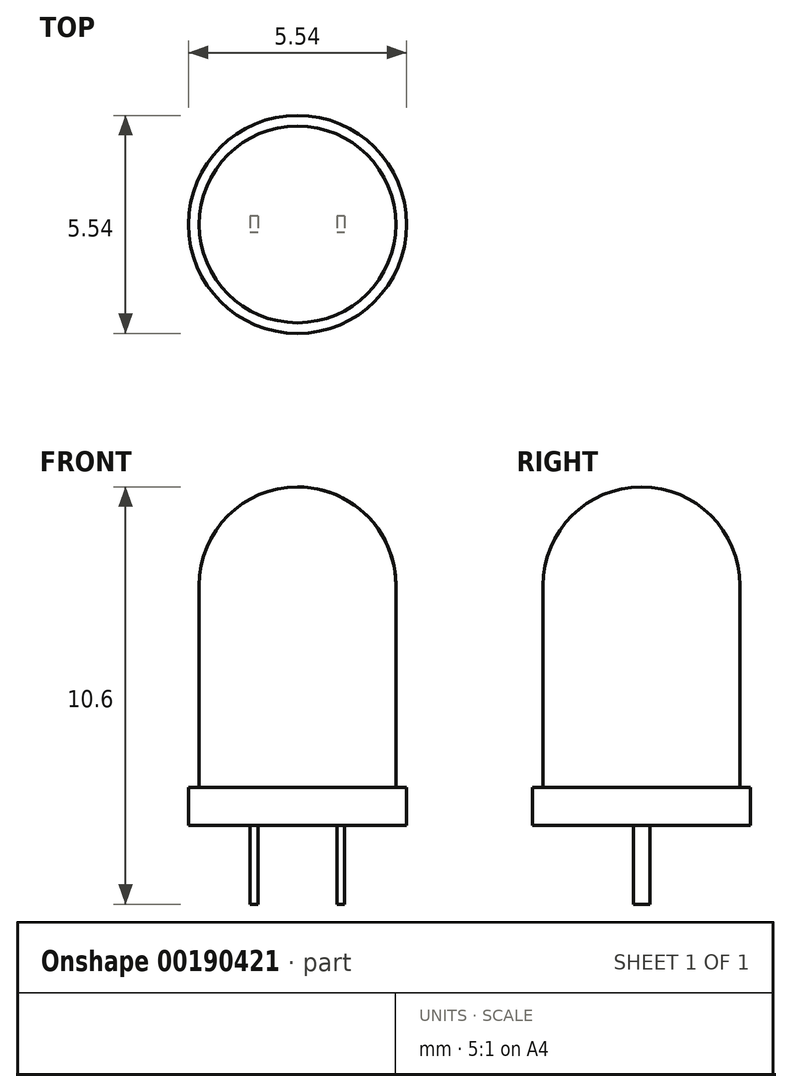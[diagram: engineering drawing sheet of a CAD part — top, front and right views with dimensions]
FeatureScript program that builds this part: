
annotation { "Feature Type Name" : "Feature", "Feature Type Description" : "" }
export const myFeature = defineFeature(function(context is Context, id is Id, definition is map)
    precondition{}
    {
        {
            var Q0;
            Q0=qCreatedBy(makeId("Top.planeOp"),FACE);
            var sketch = newSketch(context, id + "F0", { "sketchPlane" : qUnion([Q0])});
            skCircle(sketch, "E0", {"center": v(0, 0) * mm, "radius": 2.5 * mm});
            skCircle(sketch, "E1", {"center": v(0, 0) * mm, "radius": 2.77 * mm});
            skSolve(sketch);
        }
        {
            var Q0;
            Q0 = qSketchRegion(id + "F0", true);
            var Q1;
            Q1=makeQuery(id+"F0.imprint","IMPRINT",FACE,{"disambiguationData":[TD([[makeQuery(id+"F0.imprint","IMPRINT",EDGE,{"derivedFrom":sQuery(id+"F0.wireOp",EDGE,"E0")}),1.0]])]});
            extrude(context, id + "F1", {"entities" : qUnion([Q0, Q1]), "depth" : 0.97 * mm});
        }
        {
            var Q0;
            Q0=makeQuery(id+"F0.imprint","IMPRINT",FACE,{"disambiguationData":[TD([[makeQuery(id+"F0.imprint","IMPRINT",EDGE,{"derivedFrom":sQuery(id+"F0.wireOp",EDGE,"E0")}),1.0]])]});
            extrude(context, id + "F2", {"entities" : qUnion([Q0]), "operationType" : NewBodyOperationType.ADD, "depth" : 8.6 * mm});
        }
        {
            var Q0;
            Q0=makeQuery(id+"F2.opExtrude","CAP_FACE",FACE,{"disambiguationData":[OSD([sQuery(id+"F0.wireOp",EDGE,"E0")])],"isStart":false});
            fillet(context, id + "F3", {"entities" : qUnion([Q0]), "radius" : 2.5 * mm, "tangentPropagation" : true, "allowEdgeOverflow" : false});
        }
        {
            var Q0;
            Q0=makeQuery(id+"F1.opExtrude","CAP_FACE",FACE,{"disambiguationData":[OSD([sQuery(id+"F0.wireOp",EDGE,"E1")])],"isStart":true});
            var sketch = newSketch(context, id + "F4", { "sketchPlane" : qUnion([Q0])});
            skLineSegment(sketch, "E2.bottom", {"start": v(1.2, -0.2) * mm, "end": v(-1.2, -0.2) * mm});
            skLineSegment(sketch, "E2.top", {"start": v(1.2, 0.2) * mm, "end": v(-1.2, 0.2) * mm});
            skLineSegment(sketch, "E2.left", {"start": v(1.2, -0.2) * mm, "end": v(1.2, 0.2) * mm});
            skLineSegment(sketch, "E2.right", {"start": v(-1.2, -0.2) * mm, "end": v(-1.2, 0.2) * mm});
            skPoint(sketch, "E2.middle", {"position": v(0, 0) * mm});
            skLineSegment(sketch, "E3.bottom", {"start": v(1, -0.2) * mm, "end": v(-1, -0.2) * mm});
            skLineSegment(sketch, "E3.top", {"start": v(1, 0.2) * mm, "end": v(-1, 0.2) * mm});
            skLineSegment(sketch, "E3.left", {"start": v(1, -0.2) * mm, "end": v(1, 0.2) * mm});
            skLineSegment(sketch, "E3.right", {"start": v(-1, -0.2) * mm, "end": v(-1, 0.2) * mm});
            skSolve(sketch);
        }
        {
            var Q0;
            {var subQ0=sQuery(id+"F4.wireOp",EDGE,"E2.right");Q0=makeQuery(id+"F4.imprint","IMPRINT",FACE,{"disambiguationData":[TD([[makeQuery(id+"F4.imprint","IMPRINT",EDGE,{"derivedFrom":subQ0}),-1.0]])]});}
            var Q1;
            {var subQ0=sQuery(id+"F4.wireOp",EDGE,"E2.left");Q1=makeQuery(id+"F4.imprint","IMPRINT",FACE,{"disambiguationData":[TD([[makeQuery(id+"F4.imprint","IMPRINT",EDGE,{"derivedFrom":subQ0}),1.0]])]});}
            extrude(context, id + "F5", {"entities" : qUnion([Q0, Q1]), "operationType" : NewBodyOperationType.ADD, "depth" : 2 * mm});
        }
    });
